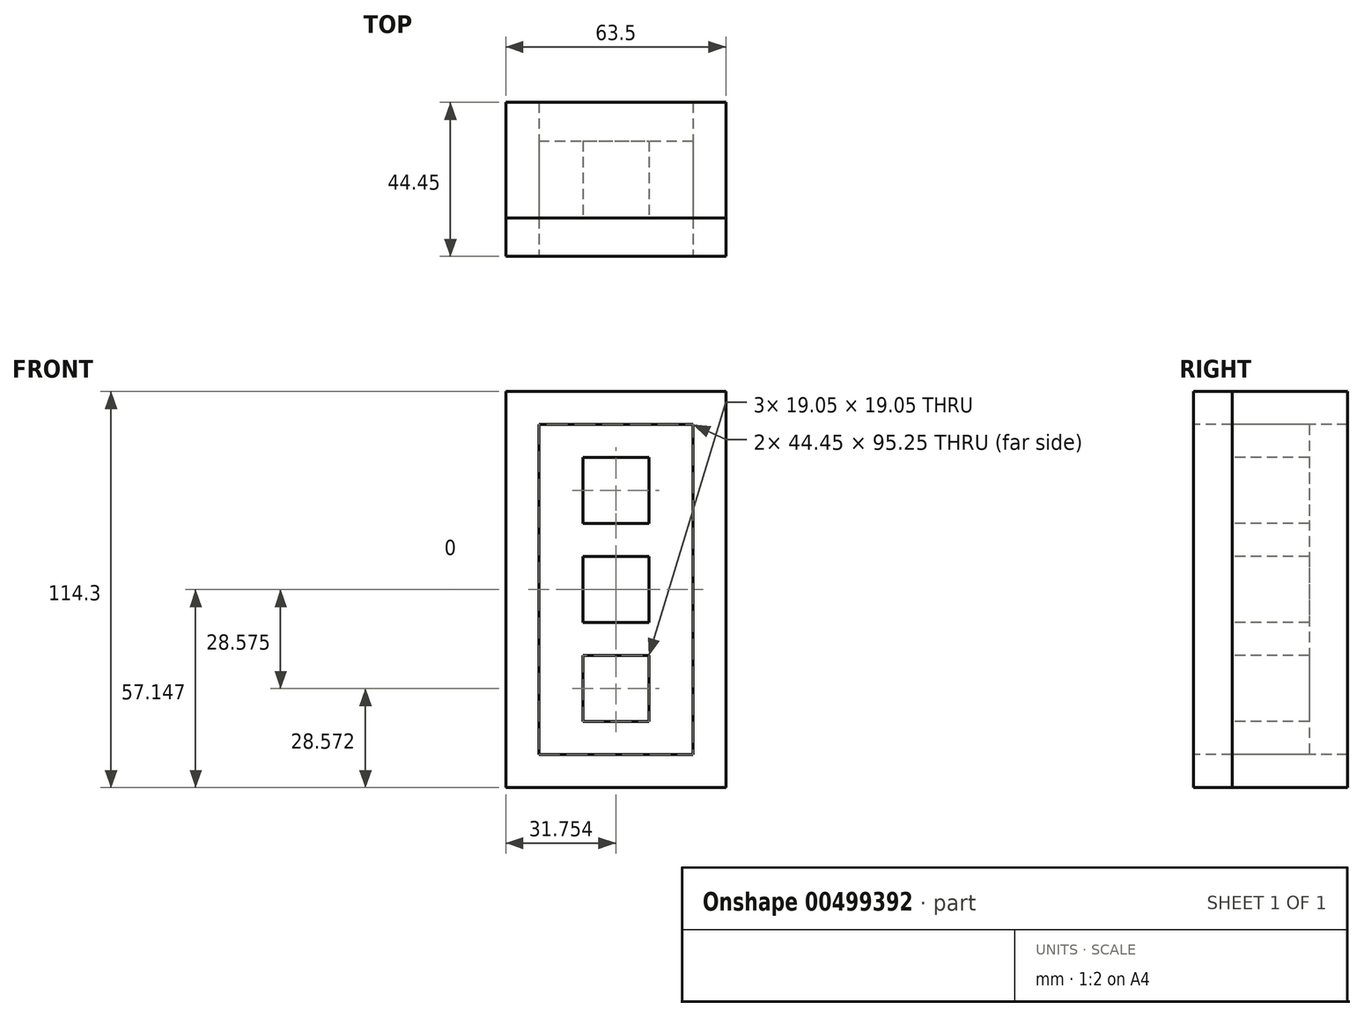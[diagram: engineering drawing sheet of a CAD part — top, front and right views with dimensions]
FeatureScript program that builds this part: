
annotation { "Feature Type Name" : "Feature", "Feature Type Description" : "" }
export const myFeature = defineFeature(function(context is Context, id is Id, definition is map)
    precondition{}
    {
        {
            var Q0;
            Q0=qCreatedBy(makeId("Front.planeOp"),FACE);
            var sketch = newSketch(context, id + "F0", { "sketchPlane" : qUnion([Q0])});
            skLineSegment(sketch, "E0", {"start": v(-42.05, 54.5) * mm, "end": v(21.45, 54.5) * mm});
            skLineSegment(sketch, "E1", {"start": v(21.45, 54.5) * mm, "end": v(21.45, -59.8) * mm});
            skLineSegment(sketch, "E2", {"start": v(21.45, -59.8) * mm, "end": v(-42.05, -59.8) * mm});
            skLineSegment(sketch, "E3", {"start": v(-42.05, -59.8) * mm, "end": v(-42.05, 54.5) * mm});
            skLineSegment(sketch, "E4", {"start": v(-32.52, 44.97) * mm, "end": v(11.93, 44.97) * mm});
            skLineSegment(sketch, "E5", {"start": v(-32.52, -50.28) * mm, "end": v(11.93, -50.28) * mm});
            skLineSegment(sketch, "E6", {"start": v(-32.52, 44.97) * mm, "end": v(-32.52, -50.28) * mm});
            skLineSegment(sketch, "E7", {"start": v(11.93, -50.28) * mm, "end": v(11.93, 44.97) * mm});
            skLineSegment(sketch, "E8", {"start": v(-42.05, 54.5) * mm, "end": v(-10.3, 54.5) * mm});
            skLineSegment(sketch, "E9.bottom", {"start": v(-19.82, 6.87) * mm, "end": v(-0.77, 6.87) * mm});
            skLineSegment(sketch, "E9.top", {"start": v(-19.82, -12.18) * mm, "end": v(-0.77, -12.18) * mm});
            skLineSegment(sketch, "E9.left", {"start": v(-19.82, 6.87) * mm, "end": v(-19.82, -12.18) * mm});
            skLineSegment(sketch, "E9.right", {"start": v(-0.77, 6.87) * mm, "end": v(-0.77, -12.18) * mm});
            skLineSegment(sketch, "E10.bottom", {"start": v(-19.82, 35.45) * mm, "end": v(-0.77, 35.45) * mm});
            skLineSegment(sketch, "E10.top", {"start": v(-19.82, 16.4) * mm, "end": v(-0.77, 16.4) * mm});
            skLineSegment(sketch, "E10.left", {"start": v(-19.82, 35.45) * mm, "end": v(-19.82, 16.4) * mm});
            skLineSegment(sketch, "E10.right", {"start": v(-0.77, 35.45) * mm, "end": v(-0.77, 16.4) * mm});
            skLineSegment(sketch, "E11.bottom", {"start": v(-19.82, -21.7) * mm, "end": v(-0.77, -21.7) * mm});
            skLineSegment(sketch, "E11.top", {"start": v(-19.82, -40.75) * mm, "end": v(-0.77, -40.75) * mm});
            skLineSegment(sketch, "E11.left", {"start": v(-19.82, -21.7) * mm, "end": v(-19.82, -40.75) * mm});
            skLineSegment(sketch, "E11.right", {"start": v(-0.77, -21.7) * mm, "end": v(-0.77, -40.75) * mm});
            skSolve(sketch);
        }
        {
            var Q0;
            Q0=makeQuery(id+"F0.imprint","IMPRINT",FACE,{"disambiguationData":[TD([[makeQuery(id+"F0.imprint","IMPRINT",EDGE,{"derivedFrom":sQuery(id+"F0.wireOp",EDGE,"E4")}),-1.0]])]});
            extrude(context, id + "F1", {"entities" : qUnion([Q0]), "oppositeDirection" : true, "depth" : 22.22 * mm});
        }
        {
            var Q0;
            Q0=makeQuery(id+"F1.opExtrude","CAP_FACE",FACE,{"disambiguationData":[OSD([sQuery(id+"F0.wireOp",EDGE,"E4"),sQuery(id+"F0.wireOp",EDGE,"E5"),sQuery(id+"F0.wireOp",EDGE,"E6"),sQuery(id+"F0.wireOp",EDGE,"E7"),sQuery(id+"F0.wireOp",EDGE,"E9.bottom"),sQuery(id+"F0.wireOp",EDGE,"E9.top"),sQuery(id+"F0.wireOp",EDGE,"E9.left"),sQuery(id+"F0.wireOp",EDGE,"E9.right"),sQuery(id+"F0.wireOp",EDGE,"E10.bottom"),sQuery(id+"F0.wireOp",EDGE,"E10.top"),sQuery(id+"F0.wireOp",EDGE,"E10.left"),sQuery(id+"F0.wireOp",EDGE,"E10.right"),sQuery(id+"F0.wireOp",EDGE,"E11.bottom"),sQuery(id+"F0.wireOp",EDGE,"E11.top"),sQuery(id+"F0.wireOp",EDGE,"E11.left"),sQuery(id+"F0.wireOp",EDGE,"E11.right")])],"isStart":true});
            var sketch = newSketch(context, id + "F2", { "sketchPlane" : qUnion([Q0])});
            skLineSegment(sketch, "E12", {"start": v(21.45, -50.28) * mm, "end": v(21.45, 44.97) * mm});
            skLineSegment(sketch, "E13", {"start": v(11.93, 44.97) * mm, "end": v(-32.52, 44.97) * mm});
            skLineSegment(sketch, "E14", {"start": v(-42.05, 44.97) * mm, "end": v(-42.05, -50.28) * mm});
            skLineSegment(sketch, "E15", {"start": v(-42.05, -50.28) * mm, "end": v(-42.05, -59.8) * mm});
            skLineSegment(sketch, "E16", {"start": v(-42.05, -59.8) * mm, "end": v(21.45, -59.8) * mm});
            skLineSegment(sketch, "E17", {"start": v(21.45, -59.8) * mm, "end": v(21.45, -50.28) * mm});
            skLineSegment(sketch, "E18", {"start": v(-42.05, 44.97) * mm, "end": v(-42.05, 54.5) * mm});
            skLineSegment(sketch, "E19", {"start": v(-42.05, 54.5) * mm, "end": v(21.45, 54.5) * mm});
            skLineSegment(sketch, "E20", {"start": v(21.45, 54.5) * mm, "end": v(21.45, 44.97) * mm});
            skSolve(sketch);
        }
        {
            var Q0;
            Q0 = qSketchRegion(id + "F2", true);
            extrude(context, id + "F3", {"entities" : qUnion([Q0]), "operationType" : NewBodyOperationType.ADD, "depth" : 11.1 * mm});
        }
        {
            var Q0;
            Q0=makeQuery(id+"F3.opExtrude","CAP_FACE",FACE,{"disambiguationData":[OSD([sQuery(id+"F2.wireOp",EDGE,"E12"),sQuery(id+"F2.wireOp",EDGE,"E14"),sQuery(id+"F2.wireOp",EDGE,"E15"),sQuery(id+"F2.wireOp",EDGE,"E16"),sQuery(id+"F2.wireOp",EDGE,"E17"),sQuery(id+"F2.wireOp",EDGE,"E18"),sQuery(id+"F2.wireOp",EDGE,"E19"),sQuery(id+"F2.wireOp",EDGE,"E20")])],"isStart":false});
            var sketch = newSketch(context, id + "F4", { "sketchPlane" : qUnion([Q0])});
            skLineSegment(sketch, "E21", {"start": v(-42.05, 54.5) * mm, "end": v(-42.05, 44.97) * mm});
            skLineSegment(sketch, "E22", {"start": v(21.45, 54.5) * mm, "end": v(21.45, 44.97) * mm});
            skLineSegment(sketch, "E23", {"start": v(21.45, 44.97) * mm, "end": v(11.93, 44.97) * mm});
            skLineSegment(sketch, "E24", {"start": v(11.93, 44.97) * mm, "end": v(21.45, 44.97) * mm});
            skLineSegment(sketch, "E25", {"start": v(-42.05, 44.97) * mm, "end": v(-32.52, 44.97) * mm});
            skLineSegment(sketch, "E26", {"start": v(-32.52, 44.97) * mm, "end": v(11.93, 44.97) * mm});
            skLineSegment(sketch, "E27", {"start": v(-42.05, -59.8) * mm, "end": v(-42.05, -50.28) * mm});
            skLineSegment(sketch, "E28", {"start": v(21.45, -59.8) * mm, "end": v(21.45, -50.28) * mm});
            skLineSegment(sketch, "E29", {"start": v(21.45, -50.28) * mm, "end": v(11.93, -50.28) * mm});
            skLineSegment(sketch, "E30", {"start": v(11.93, -50.28) * mm, "end": v(-32.52, -50.28) * mm});
            skLineSegment(sketch, "E31", {"start": v(-32.52, -50.28) * mm, "end": v(-42.05, -50.28) * mm});
            skLineSegment(sketch, "E32", {"start": v(-32.52, -50.28) * mm, "end": v(-32.52, 44.97) * mm});
            skLineSegment(sketch, "E33", {"start": v(11.93, 44.97) * mm, "end": v(11.93, -50.28) * mm});
            skSolve(sketch);
        }
        {
            var Q0;
            Q0=makeQuery(id+"F4.imprint","IMPRINT",FACE,{"disambiguationData":[TD([[makeQuery(id+"F4.imprint","IMPRINT",EDGE,{"derivedFrom":sQuery(id+"F4.wireOp",EDGE,"E26")}),-1.0]])]});
            extrude(context, id + "F5", {"entities" : qUnion([Q0]), "operationType" : NewBodyOperationType.REMOVE, "oppositeDirection" : true, "depth" : 11.1 * mm});
        }
        {
            var Q0;
            {var subQ0=sQuery(id+"F2.wireOp",EDGE,"E18");var subQ1=sQuery(id+"F2.wireOp",EDGE,"E15");var subQ2=sQuery(id+"F2.wireOp",EDGE,"E14");var subQ3=sQuery(id+"F2.wireOp",EDGE,"E20");var subQ4=sQuery(id+"F2.wireOp",EDGE,"E17");var subQ5=sQuery(id+"F2.wireOp",EDGE,"E12");var subQ6=sQuery(id+"F2.wireOp",EDGE,"E16");var subQ7=sQuery(id+"F2.wireOp",EDGE,"E19");Q0=makeQuery(id+"F3.boolean.opBoolean","SPLIT",FACE,{"disambiguationData":[TD([makeQuery(id+"F1.opExtrude","SWEPT_FACE",FACE,{"disambiguationData":[OSD([sQuery(id+"F0.wireOp",EDGE,"E4")])]})])],"derivedFrom":makeQuery(id+"F3.opExtrude","CAP_FACE",FACE,{"disambiguationData":[OSD([subQ5,subQ2,subQ1,subQ6,subQ4,subQ0,subQ7,subQ3])],"isStart":true})});}
            var sketch = newSketch(context, id + "F6", { "sketchPlane" : qUnion([Q0])});
            skLineSegment(sketch, "E34", {"start": v(-21.45, 54.5) * mm, "end": v(-21.45, -59.8) * mm});
            skLineSegment(sketch, "E35", {"start": v(-21.45, -59.8) * mm, "end": v(42.05, -59.8) * mm});
            skLineSegment(sketch, "E36", {"start": v(42.05, -59.8) * mm, "end": v(42.05, 54.5) * mm});
            skLineSegment(sketch, "E37", {"start": v(42.05, 54.5) * mm, "end": v(-21.45, 54.5) * mm});
            skLineSegment(sketch, "E38", {"start": v(-11.93, 44.97) * mm, "end": v(-11.93, -50.28) * mm});
            skLineSegment(sketch, "E39", {"start": v(-11.93, -50.28) * mm, "end": v(32.52, -50.28) * mm});
            skLineSegment(sketch, "E40", {"start": v(32.52, -50.28) * mm, "end": v(32.52, 44.97) * mm});
            skLineSegment(sketch, "E41", {"start": v(32.52, 44.97) * mm, "end": v(-11.93, 44.97) * mm});
            skSolve(sketch);
        }
        {
            var Q0;
            Q0=makeQuery(id+"F6.imprint","IMPRINT",FACE,{"disambiguationData":[TD([[makeQuery(id+"F6.imprint","IMPRINT",EDGE,{"derivedFrom":sQuery(id+"F6.wireOp",EDGE,"E34")}),-1.0]])]});
            extrude(context, id + "F7", {"entities" : qUnion([Q0]), "depth" : 33.34 * mm});
        }
    });
